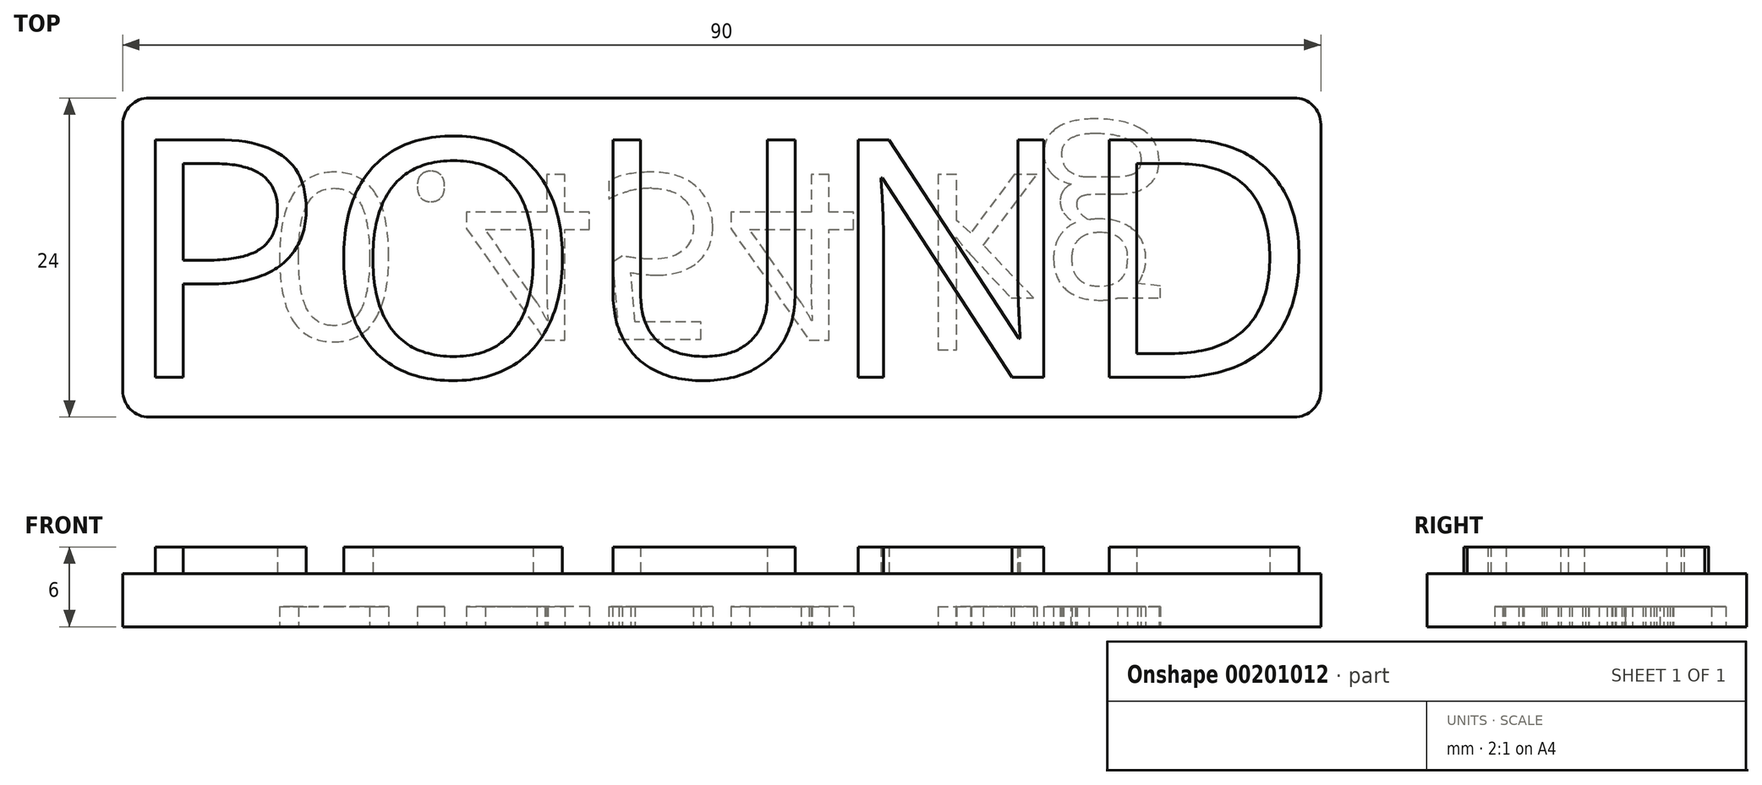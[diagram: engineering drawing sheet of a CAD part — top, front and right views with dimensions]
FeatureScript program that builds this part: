
annotation { "Feature Type Name" : "Feature", "Feature Type Description" : "" }
export const myFeature = defineFeature(function(context is Context, id is Id, definition is map)
    precondition{}
    {
        {
            var Q0;
            Q0=qCreatedBy(makeId("Top.planeOp"),FACE);
            var sketch = newSketch(context, id + "F0", { "sketchPlane" : qUnion([Q0])});
            skLineSegment(sketch, "E0.bottom", {"start": v(-45, 12) * mm, "end": v(45, 12) * mm});
            skLineSegment(sketch, "E0.top", {"start": v(-45, -12) * mm, "end": v(45, -12) * mm});
            skLineSegment(sketch, "E0.left", {"start": v(-45, 12) * mm, "end": v(-45, -12) * mm});
            skLineSegment(sketch, "E0.right", {"start": v(45, 12) * mm, "end": v(45, -12) * mm});
            skLineSegment(sketch, "E1", {"start": v(0, -12) * mm, "end": v(0, 12) * mm, "construction": true});
            skSolve(sketch);
        }
        {
            var Q0;
            Q0=makeQuery(id+"F0.imprint","IMPRINT",FACE,{"disambiguationData":[TD([[makeQuery(id+"F0.imprint","IMPRINT",EDGE,{"derivedFrom":sQuery(id+"F0.wireOp",EDGE,"E0.bottom")}),-1.0]])]});
            extrude(context, id + "F1", {"entities" : qUnion([Q0]), "depth" : 4 * mm});
        }
        {
            var Q0;
            Q0=makeQuery(id+"F1.opExtrude","SWEPT_EDGE",EDGE,{"disambiguationData":[OSD([sQuery(id+"F0.wireOp",EDGE,"E0.top"),sQuery(id+"F0.wireOp",EDGE,"E0.left")])]});
            var Q1;
            Q1=makeQuery(id+"F1.opExtrude","SWEPT_EDGE",EDGE,{"disambiguationData":[OSD([sQuery(id+"F0.wireOp",EDGE,"E0.bottom"),sQuery(id+"F0.wireOp",EDGE,"E0.right")])]});
            var Q2;
            Q2=makeQuery(id+"F1.opExtrude","SWEPT_EDGE",EDGE,{"disambiguationData":[OSD([sQuery(id+"F0.wireOp",EDGE,"E0.bottom"),sQuery(id+"F0.wireOp",EDGE,"E0.left")])]});
            var Q3;
            Q3=makeQuery(id+"F1.opExtrude","SWEPT_EDGE",EDGE,{"disambiguationData":[OSD([sQuery(id+"F0.wireOp",EDGE,"E0.top"),sQuery(id+"F0.wireOp",EDGE,"E0.right")])]});
            fillet(context, id + "F2", {"entities" : qUnion([Q0, Q1, Q2, Q3]), "radius" : 2 * mm, "tangentPropagation" : true, "allowEdgeOverflow" : false});
        }
        {
            var Q0;
            Q0=makeQuery(id+"F1.opExtrude","CAP_FACE",FACE,{"disambiguationData":[OSD([sQuery(id+"F0.wireOp",EDGE,"E0.bottom"),sQuery(id+"F0.wireOp",EDGE,"E0.top"),sQuery(id+"F0.wireOp",EDGE,"E0.left"),sQuery(id+"F0.wireOp",EDGE,"E0.right")])],"isStart":false});
            var sketch = newSketch(context, id + "F3", { "sketchPlane" : qUnion([Q0])});
            skText(sketch, "E2", { "text": "POUND", "fontName": "OpenSans-Regular.ttf"});
            const initialGuessF3  = {"E2": [-0.045, -0.00901, 1, 0, 0.01802]};
            skSetInitialGuess(sketch, initialGuessF3);
            skSolve(sketch);
        }
        {
            var Q0;
            {var subQ0=sQuery(id+"F3.wireOp",EDGE,"E2.sketch_text.stroke-4");Q0=makeQuery(id+"F3.imprint","IMPRINT",FACE,{"disambiguationData":[TD([[makeQuery(id+"F3.imprint","IMPRINT",EDGE,{"derivedFrom":subQ0}),-1.0]])]});}
            var Q1;
            {var subQ0=sQuery(id+"F3.wireOp",EDGE,"E2.sketch_text.stroke-3");var subQ1=sQuery(id+"F3.wireOp",EDGE,"E2.sketch_text.stroke-2");var subQ2=makeQuery(id+"F3.imprint","INTERSECT",VERTEX,{"derivedFrom":[subQ1,subQ0]});Q1=makeQuery(id+"F3.imprint","IMPRINT",FACE,{"disambiguationData":[TD([[makeQuery(id+"F3.imprint","IMPRINT",EDGE,{"disambiguationData":[TD([[subQ2,1.0]])],"derivedFrom":subQ1}),-1.0]])]});}
            var Q2;
            {var subQ1=sQuery(id+"F3.wireOp",EDGE,"E2.sketch_text.stroke-1");Q2=makeQuery(id+"F3.imprint","IMPRINT",FACE,{"disambiguationData":[TD([[makeQuery(id+"F3.imprint","IMPRINT",EDGE,{"derivedFrom":subQ1}),-1.0]])]});}
            var Q3;
            {var subQ0=sQuery(id+"F3.wireOp",EDGE,"E2.sketch_text.stroke-0");var subQ1=makeQuery(id+"F1.opExtrude","CAP_EDGE",EDGE,{"disambiguationData":[OSD([sQuery(id+"F0.wireOp",EDGE,"E0.top")])],"isStart":false});var subQ2=makeQuery(id+"F3.imprint","INTERSECT",VERTEX,{"derivedFrom":[subQ1,subQ0]});Q3=makeQuery(id+"F3.imprint","IMPRINT",FACE,{"disambiguationData":[TD([[makeQuery(id+"F3.imprint","IMPRINT",EDGE,{"disambiguationData":[TD([[subQ2,-1.0]])],"derivedFrom":subQ0}),-1.0]])]});}
            var Q4;
            {var subQ1=sQuery(id+"F3.wireOp",EDGE,"E2.sketch_text.stroke-8");Q4=makeQuery(id+"F3.imprint","IMPRINT",FACE,{"disambiguationData":[TD([[makeQuery(id+"F3.imprint","IMPRINT",EDGE,{"derivedFrom":subQ1}),-1.0]])]});}
            var Q5;
            {var subQ0=sQuery(id+"F3.wireOp",EDGE,"E2.sketch_text.stroke-9");var subQ1=makeQuery(id+"F1.opExtrude","CAP_EDGE",EDGE,{"disambiguationData":[OSD([sQuery(id+"F0.wireOp",EDGE,"E0.bottom")])],"isStart":false});var subQ2=makeQuery(id+"F3.imprint","INTERSECT",VERTEX,{"derivedFrom":[subQ1,subQ0]});Q5=makeQuery(id+"F3.imprint","IMPRINT",FACE,{"disambiguationData":[TD([[makeQuery(id+"F3.imprint","IMPRINT",EDGE,{"disambiguationData":[TD([[subQ2,1.0]])],"derivedFrom":subQ0}),-1.0]])]});}
            var Q6;
            {var subQ1=sQuery(id+"F3.wireOp",EDGE,"E2.sketch_text.stroke-10");Q6=makeQuery(id+"F3.imprint","IMPRINT",FACE,{"disambiguationData":[TD([[makeQuery(id+"F3.imprint","IMPRINT",EDGE,{"derivedFrom":subQ1}),-1.0]])]});}
            var Q7;
            {var subQ0=sQuery(id+"F3.wireOp",EDGE,"E2.sketch_text.stroke-11");var subQ1=makeQuery(id+"F1.opExtrude","CAP_EDGE",EDGE,{"disambiguationData":[OSD([sQuery(id+"F0.wireOp",EDGE,"E0.bottom")])],"isStart":false});var subQ2=makeQuery(id+"F3.imprint","INTERSECT",VERTEX,{"derivedFrom":[subQ1,subQ0]});Q7=makeQuery(id+"F3.imprint","IMPRINT",FACE,{"disambiguationData":[TD([[makeQuery(id+"F3.imprint","IMPRINT",EDGE,{"disambiguationData":[TD([[subQ2,-1.0]])],"derivedFrom":subQ0}),-1.0]])]});}
            var Q8;
            {var subQ0=sQuery(id+"F3.wireOp",EDGE,"E2.sketch_text.stroke-12");Q8=makeQuery(id+"F3.imprint","IMPRINT",FACE,{"disambiguationData":[TD([[makeQuery(id+"F3.imprint","IMPRINT",EDGE,{"derivedFrom":subQ0}),-1.0]])]});}
            var Q9;
            {var subQ0=sQuery(id+"F3.wireOp",EDGE,"E2.sketch_text.stroke-21");Q9=makeQuery(id+"F3.imprint","IMPRINT",FACE,{"disambiguationData":[TD([[makeQuery(id+"F3.imprint","IMPRINT",EDGE,{"derivedFrom":subQ0}),-1.0]])]});}
            var Q10;
            {var subQ0=sQuery(id+"F3.wireOp",EDGE,"E2.sketch_text.stroke-18");var subQ1=makeQuery(id+"F1.opExtrude","CAP_EDGE",EDGE,{"disambiguationData":[OSD([sQuery(id+"F0.wireOp",EDGE,"E0.top")])],"isStart":false});var subQ2=makeQuery(id+"F3.imprint","INTERSECT",VERTEX,{"derivedFrom":[subQ1,subQ0]});Q10=makeQuery(id+"F3.imprint","IMPRINT",FACE,{"disambiguationData":[TD([[makeQuery(id+"F3.imprint","IMPRINT",EDGE,{"disambiguationData":[TD([[subQ2,-1.0]])],"derivedFrom":subQ0}),-1.0]])]});}
            var Q11;
            {var subQ0=sQuery(id+"F3.wireOp",EDGE,"E2.sketch_text.stroke-19");Q11=makeQuery(id+"F3.imprint","IMPRINT",FACE,{"disambiguationData":[TD([[makeQuery(id+"F3.imprint","IMPRINT",EDGE,{"derivedFrom":subQ0}),-1.0]])]});}
            var Q12;
            {var subQ0=sQuery(id+"F3.wireOp",EDGE,"E2.sketch_text.stroke-25");Q12=makeQuery(id+"F3.imprint","IMPRINT",FACE,{"disambiguationData":[TD([[makeQuery(id+"F3.imprint","IMPRINT",EDGE,{"derivedFrom":subQ0}),-1.0]])]});}
            var Q13;
            {var subQ0=sQuery(id+"F3.wireOp",EDGE,"E2.sketch_text.stroke-22");var subQ1=makeQuery(id+"F1.opExtrude","CAP_EDGE",EDGE,{"disambiguationData":[OSD([sQuery(id+"F0.wireOp",EDGE,"E0.top")])],"isStart":false});var subQ2=makeQuery(id+"F3.imprint","INTERSECT",VERTEX,{"derivedFrom":[subQ1,subQ0]});Q13=makeQuery(id+"F3.imprint","IMPRINT",FACE,{"disambiguationData":[TD([[makeQuery(id+"F3.imprint","IMPRINT",EDGE,{"disambiguationData":[TD([[subQ2,-1.0]])],"derivedFrom":subQ0}),-1.0]])]});}
            var Q14;
            {var subQ0=sQuery(id+"F3.wireOp",EDGE,"E2.sketch_text.stroke-23");Q14=makeQuery(id+"F3.imprint","IMPRINT",FACE,{"disambiguationData":[TD([[makeQuery(id+"F3.imprint","IMPRINT",EDGE,{"derivedFrom":subQ0}),-1.0]])]});}
            var Q15;
            {var subQ5=sQuery(id+"F3.wireOp",EDGE,"E2.sketch_text.stroke-28");Q15=makeQuery(id+"F3.imprint","IMPRINT",FACE,{"disambiguationData":[TD([[makeQuery(id+"F3.imprint","IMPRINT",EDGE,{"derivedFrom":subQ5}),-1.0]])]});}
            var Q16;
            {var subQ0=sQuery(id+"F3.wireOp",EDGE,"E2.sketch_text.stroke-34");Q16=makeQuery(id+"F3.imprint","IMPRINT",FACE,{"disambiguationData":[TD([[makeQuery(id+"F3.imprint","IMPRINT",EDGE,{"derivedFrom":subQ0}),-1.0]])]});}
            var Q17;
            {var subQ0=sQuery(id+"F3.wireOp",EDGE,"E2.sketch_text.stroke-30");Q17=makeQuery(id+"F3.imprint","IMPRINT",FACE,{"disambiguationData":[TD([[makeQuery(id+"F3.imprint","IMPRINT",EDGE,{"derivedFrom":subQ0}),-1.0]])]});}
            var Q18;
            {var subQ0=sQuery(id+"F3.wireOp",EDGE,"E2.sketch_text.stroke-6");Q18=makeQuery(id+"F3.imprint","IMPRINT",FACE,{"disambiguationData":[TD([[makeQuery(id+"F3.imprint","IMPRINT",EDGE,{"derivedFrom":subQ0}),-1.0]])]});}
            var Q19;
            {var subQ0=sQuery(id+"F3.wireOp",EDGE,"E2.sketch_text.stroke-17");Q19=makeQuery(id+"F3.imprint","IMPRINT",FACE,{"disambiguationData":[TD([[makeQuery(id+"F3.imprint","IMPRINT",EDGE,{"derivedFrom":subQ0}),-1.0]])]});}
            var Q20;
            {var subQ0=sQuery(id+"F3.wireOp",EDGE,"E2.sketch_text.stroke-27");Q20=makeQuery(id+"F3.imprint","IMPRINT",FACE,{"disambiguationData":[TD([[makeQuery(id+"F3.imprint","IMPRINT",EDGE,{"derivedFrom":subQ0}),-1.0]])]});}
            var Q21;
            Q21=makeQuery(id+"F3.imprint","IMPRINT",FACE,{"disambiguationData":[TD([[makeQuery(id+"F3.imprint","IMPRINT",EDGE,{"derivedFrom":sQuery(id+"F3.wireOp",EDGE,"E2.sketch_text.stroke-45")}),-1.0]])]});
            var Q22;
            Q22=makeQuery(id+"F3.imprint","IMPRINT",FACE,{"disambiguationData":[TD([[makeQuery(id+"F3.imprint","IMPRINT",EDGE,{"derivedFrom":sQuery(id+"F3.wireOp",EDGE,"E2.sketch_text.stroke-60")}),-1.0]])]});
            extrude(context, id + "F4", {"entities" : qUnion([Q0, Q1, Q2, Q3, Q4, Q5, Q6, Q7, Q8, Q9, Q10, Q11, Q12, Q13, Q14, Q15, Q16, Q17, Q18, Q19, Q20, Q21, Q22]), "operationType" : NewBodyOperationType.ADD, "depth" : 2 * mm});
        }
        {
            var Q0;
            Q0=makeQuery(id+"F1.opExtrude","CAP_FACE",FACE,{"disambiguationData":[OSD([sQuery(id+"F0.wireOp",EDGE,"E0.bottom"),sQuery(id+"F0.wireOp",EDGE,"E0.top"),sQuery(id+"F0.wireOp",EDGE,"E0.left"),sQuery(id+"F0.wireOp",EDGE,"E0.right")])],"isStart":true});
            var sketch = newSketch(context, id + "F5", { "sketchPlane" : qUnion([Q0])});
            skText(sketch, "E3", { "text": "0.454 kg", "fontName": "OpenSans-Regular.ttf"});
            const initialGuessF5  = {"E3": [-0.03408, -0.00625, 1, 0, 0.0125]};
            skSetInitialGuess(sketch, initialGuessF5);
            skSolve(sketch);
        }
        {
            var Q0;
            Q0=makeQuery(id+"F5.imprint","IMPRINT",FACE,{"disambiguationData":[TD([[makeQuery(id+"F5.imprint","IMPRINT",EDGE,{"derivedFrom":sQuery(id+"F5.wireOp",EDGE,"E3.sketch_text.stroke-141")}),-1.0]])]});
            var Q1;
            Q1=makeQuery(id+"F5.imprint","IMPRINT",FACE,{"disambiguationData":[TD([[makeQuery(id+"F5.imprint","IMPRINT",EDGE,{"derivedFrom":sQuery(id+"F5.wireOp",EDGE,"E3.sketch_text.stroke-122")}),-1.0]])]});
            var Q2;
            Q2=makeQuery(id+"F5.imprint","IMPRINT",FACE,{"disambiguationData":[TD([[makeQuery(id+"F5.imprint","IMPRINT",EDGE,{"derivedFrom":sQuery(id+"F5.wireOp",EDGE,"E3.sketch_text.stroke-103")}),-1.0]])]});
            var Q3;
            Q3=makeQuery(id+"F5.imprint","IMPRINT",FACE,{"disambiguationData":[TD([[makeQuery(id+"F5.imprint","IMPRINT",EDGE,{"derivedFrom":sQuery(id+"F5.wireOp",EDGE,"E3.sketch_text.stroke-86")}),-1.0]])]});
            var Q4;
            Q4=makeQuery(id+"F5.imprint","IMPRINT",FACE,{"disambiguationData":[TD([[makeQuery(id+"F5.imprint","IMPRINT",EDGE,{"derivedFrom":sQuery(id+"F5.wireOp",EDGE,"E3.sketch_text.stroke-70")}),-1.0]])]});
            var Q5;
            Q5=makeQuery(id+"F5.imprint","IMPRINT",FACE,{"disambiguationData":[TD([[makeQuery(id+"F5.imprint","IMPRINT",EDGE,{"derivedFrom":sQuery(id+"F5.wireOp",EDGE,"E3.sketch_text.stroke-39")}),-1.0]])]});
            var Q6;
            Q6=makeQuery(id+"F5.imprint","IMPRINT",FACE,{"disambiguationData":[TD([[makeQuery(id+"F5.imprint","IMPRINT",EDGE,{"derivedFrom":sQuery(id+"F5.wireOp",EDGE,"E3.sketch_text.stroke-19")}),-1.0]])]});
            var Q7;
            Q7=makeQuery(id+"F5.imprint","IMPRINT",FACE,{"disambiguationData":[TD([[makeQuery(id+"F5.imprint","IMPRINT",EDGE,{"derivedFrom":sQuery(id+"F5.wireOp",EDGE,"E3.sketch_text.stroke-0")}),-1.0]])]});
            var Q8;
            Q8=makeQuery(id+"F5.imprint","IMPRINT",FACE,{"disambiguationData":[TD([[makeQuery(id+"F5.imprint","IMPRINT",EDGE,{"derivedFrom":sQuery(id+"F5.wireOp",EDGE,"E3.sketch_text.stroke-51")}),-1.0]])]});
            extrude(context, id + "F6", {"entities" : qUnion([Q0, Q1, Q2, Q3, Q4, Q5, Q6, Q7, Q8]), "operationType" : NewBodyOperationType.REMOVE, "oppositeDirection" : true, "depth" : 1.5 * mm});
        }
    });
